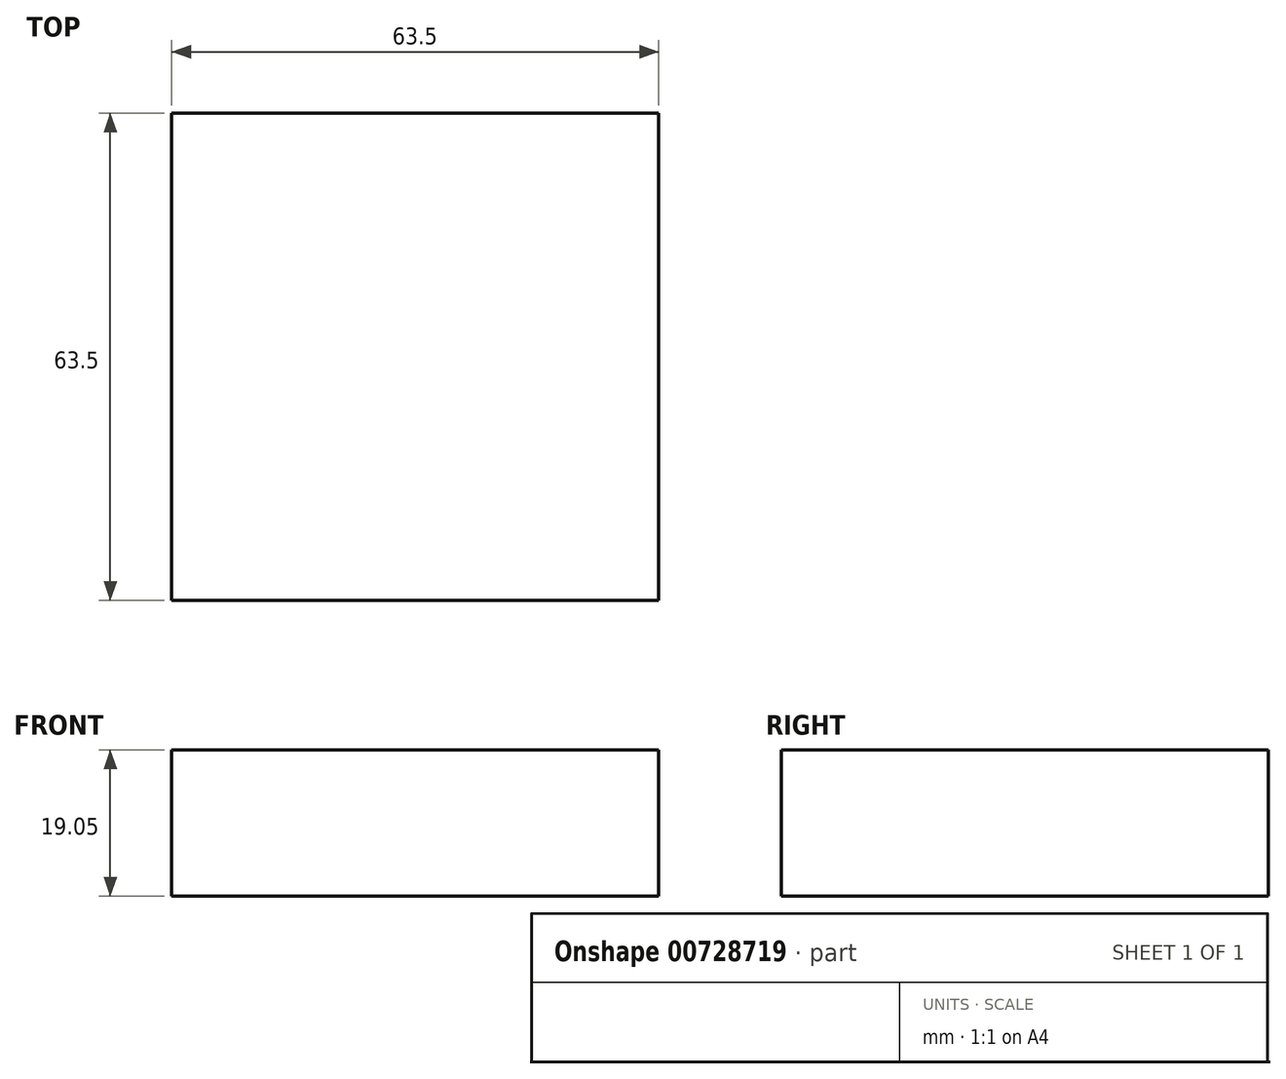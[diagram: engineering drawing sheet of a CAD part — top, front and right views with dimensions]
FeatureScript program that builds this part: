
annotation { "Feature Type Name" : "Feature", "Feature Type Description" : "" }
export const myFeature = defineFeature(function(context is Context, id is Id, definition is map)
    precondition{}
    {
        {
            var Q0;
            Q0=qCreatedBy(makeId("Top.planeOp"),FACE);
            var sketch = newSketch(context, id + "F0", { "sketchPlane" : qUnion([Q0])});
            skLineSegment(sketch, "E0.bottom", {"start": v(31.75, 31.75) * mm, "end": v(-31.75, 31.75) * mm});
            skLineSegment(sketch, "E0.top", {"start": v(31.75, -31.75) * mm, "end": v(-31.75, -31.75) * mm});
            skLineSegment(sketch, "E0.left", {"start": v(31.75, 31.75) * mm, "end": v(31.75, -31.75) * mm});
            skLineSegment(sketch, "E0.right", {"start": v(-31.75, 31.75) * mm, "end": v(-31.75, -31.75) * mm});
            skPoint(sketch, "E0.middle", {"position": v(0, 0) * mm});
            skSolve(sketch);
        }
        {
            var Q0;
            Q0 = qSketchRegion(id + "F0", true);
            extrude(context, id + "F1", {"entities" : qUnion([Q0]), "depth" : 19.05 * mm, "offsetDistance" : 25.4 * mm});
        }
    });
